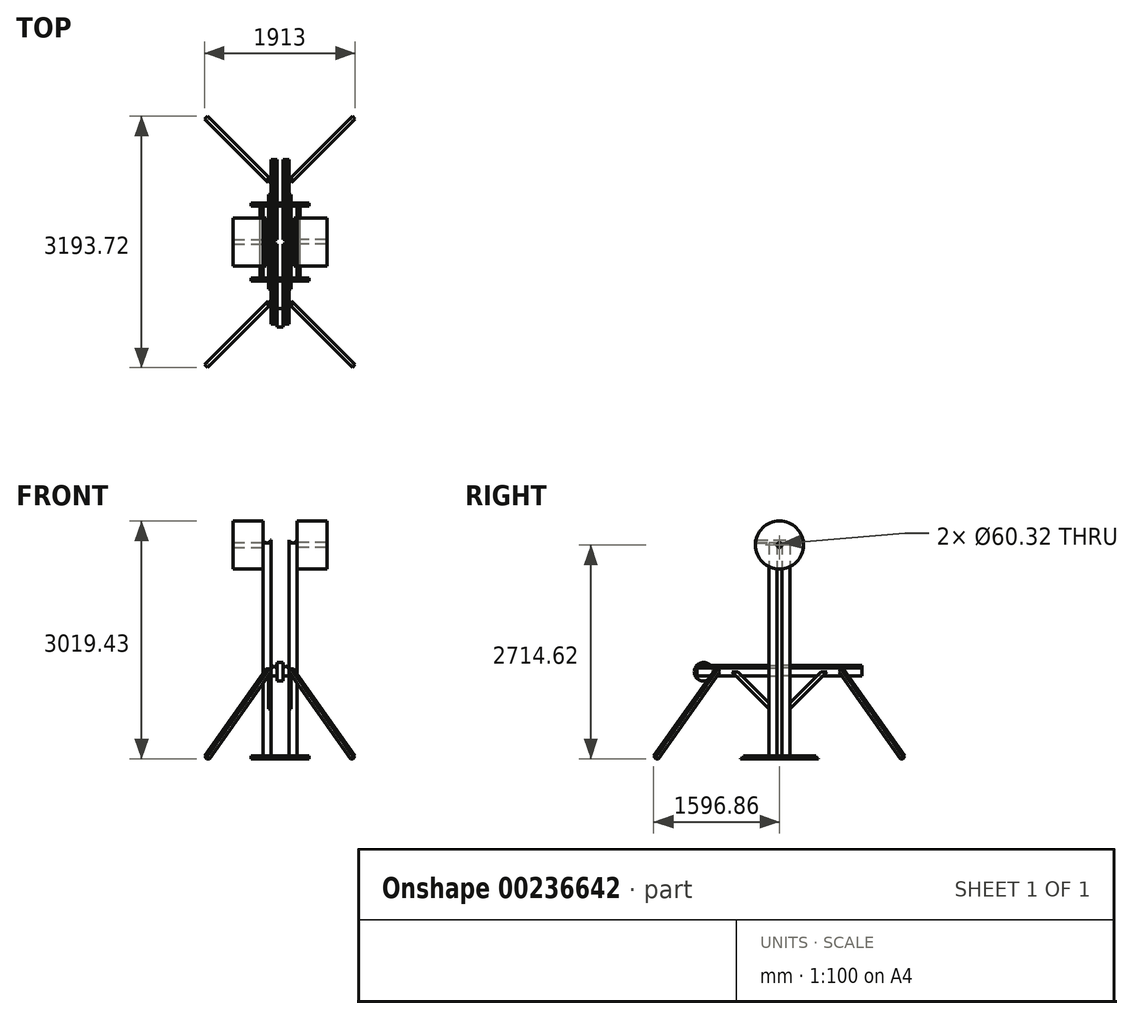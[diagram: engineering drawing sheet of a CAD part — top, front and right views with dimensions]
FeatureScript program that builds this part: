
annotation { "Feature Type Name" : "Feature", "Feature Type Description" : "" }
export const myFeature = defineFeature(function(context is Context, id is Id, definition is map)
    precondition{}
    {
        {
            var Q0;
            Q0=qCreatedBy(makeId("Top.planeOp"),FACE);
            var sketch = newSketch(context, id + "F0", { "sketchPlane" : qUnion([Q0])});
            skLineSegment(sketch, "E0.bottom", {"start": v(114.3, 30.16) * mm, "end": v(215.9, 30.16) * mm});
            skLineSegment(sketch, "E0.top", {"start": v(114.3, 131.76) * mm, "end": v(215.9, 131.76) * mm});
            skLineSegment(sketch, "E0.left", {"start": v(114.3, 30.16) * mm, "end": v(114.3, 131.76) * mm});
            skLineSegment(sketch, "E0.right", {"start": v(215.9, 30.16) * mm, "end": v(215.9, 131.76) * mm});
            skLineSegment(sketch, "E1.MirrorCS", {"start": v(-114.3, 30.16) * mm, "end": v(-215.9, 30.16) * mm});
            skLineSegment(sketch, "E2.MirrorCS", {"start": v(-114.3, 131.76) * mm, "end": v(-215.9, 131.76) * mm});
            skLineSegment(sketch, "E3.MirrorCS", {"start": v(-114.3, 30.16) * mm, "end": v(-114.3, 131.76) * mm});
            skLineSegment(sketch, "E4.MirrorCS", {"start": v(-215.9, 30.16) * mm, "end": v(-215.9, 131.76) * mm});
            skLineSegment(sketch, "E5.MirrorCS", {"start": v(-215.9, -30.16) * mm, "end": v(-215.9, -131.76) * mm});
            skLineSegment(sketch, "E6.MirrorCS", {"start": v(-114.3, -30.16) * mm, "end": v(-114.3, -131.76) * mm});
            skLineSegment(sketch, "E7.MirrorCS", {"start": v(114.3, -30.16) * mm, "end": v(215.9, -30.16) * mm});
            skLineSegment(sketch, "E8.MirrorCS", {"start": v(-114.3, -131.76) * mm, "end": v(-215.9, -131.76) * mm});
            skLineSegment(sketch, "E9.MirrorCS", {"start": v(-114.3, -30.16) * mm, "end": v(-215.9, -30.16) * mm});
            skLineSegment(sketch, "E10.MirrorCS", {"start": v(215.9, -30.16) * mm, "end": v(215.9, -131.76) * mm});
            skLineSegment(sketch, "E11.MirrorCS", {"start": v(114.3, -131.76) * mm, "end": v(215.9, -131.76) * mm});
            skLineSegment(sketch, "E12.MirrorCS", {"start": v(114.3, -30.16) * mm, "end": v(114.3, -131.76) * mm});
            skSolve(sketch);
        }
        {
            var Q0;
            Q0=makeQuery(id+"F0.imprint","IMPRINT",FACE,{"disambiguationData":[TD([[makeQuery(id+"F0.imprint","IMPRINT",EDGE,{"derivedFrom":sQuery(id+"F0.wireOp",EDGE,"E5.MirrorCS")}),1.0]])]});
            var Q1;
            Q1=makeQuery(id+"F0.imprint","IMPRINT",FACE,{"disambiguationData":[TD([[makeQuery(id+"F0.imprint","IMPRINT",EDGE,{"derivedFrom":sQuery(id+"F0.wireOp",EDGE,"E1.MirrorCS")}),-1.0]])]});
            var Q2;
            Q2=makeQuery(id+"F0.imprint","IMPRINT",FACE,{"disambiguationData":[TD([[makeQuery(id+"F0.imprint","IMPRINT",EDGE,{"derivedFrom":sQuery(id+"F0.wireOp",EDGE,"E0.bottom")}),1.0]])]});
            var Q3;
            Q3=makeQuery(id+"F0.imprint","IMPRINT",FACE,{"disambiguationData":[TD([[makeQuery(id+"F0.imprint","IMPRINT",EDGE,{"derivedFrom":sQuery(id+"F0.wireOp",EDGE,"E7.MirrorCS")}),-1.0]])]});
            extrude(context, id + "F1", {"entities" : qUnion([Q0, Q1, Q2, Q3]), "depth" : 2743.2 * mm});
        }
        {
            var Q0;
            Q0=makeQuery(id+"F1.opExtrude","SWEPT_FACE",FACE,{"disambiguationData":[OSD([sQuery(id+"F0.wireOp",EDGE,"E0.bottom")])]});
            var sketch = newSketch(context, id + "F2", { "sketchPlane" : qUnion([Q0])});
            skLineSegment(sketch, "E13.bottom", {"start": v(114.3, 1155.7) * mm, "end": v(38.1, 1155.7) * mm});
            skLineSegment(sketch, "E13.top", {"start": v(114.3, 1054.1) * mm, "end": v(38.1, 1054.1) * mm});
            skLineSegment(sketch, "E13.left", {"start": v(114.3, 1155.7) * mm, "end": v(114.3, 1054.1) * mm});
            skLineSegment(sketch, "E13.right", {"start": v(38.1, 1155.7) * mm, "end": v(38.1, 1054.1) * mm});
            skLineSegment(sketch, "E14", {"start": v(0, 1227.15) * mm, "end": v(0, 1056.68) * mm, "construction": true});
            skLineSegment(sketch, "E15.MirrorCS", {"start": v(-114.3, 1155.7) * mm, "end": v(-38.1, 1155.7) * mm});
            skLineSegment(sketch, "E16.MirrorCS", {"start": v(-114.3, 1054.1) * mm, "end": v(-38.1, 1054.1) * mm});
            skLineSegment(sketch, "E17.MirrorCS", {"start": v(-114.3, 1155.7) * mm, "end": v(-114.3, 1054.1) * mm});
            skLineSegment(sketch, "E18.MirrorCS", {"start": v(-38.1, 1155.7) * mm, "end": v(-38.1, 1054.1) * mm});
            skLineSegment(sketch, "E19", {"start": v(47.72, 1155.7) * mm, "end": v(74.66, 1182.64) * mm});
            skLineSegment(sketch, "E20", {"start": v(74.66, 1182.64) * mm, "end": v(101.6, 1155.7) * mm});
            skLineSegment(sketch, "E21.MirrorCS", {"start": v(-47.72, 1155.7) * mm, "end": v(-74.66, 1182.64) * mm});
            skLineSegment(sketch, "E22.MirrorCS", {"start": v(-74.66, 1182.64) * mm, "end": v(-101.6, 1155.7) * mm});
            skSolve(sketch);
        }
        {
            var Q0;
            Q0=makeQuery(id+"F2.imprint","IMPRINT",FACE,{"disambiguationData":[TD([[makeQuery(id+"F2.imprint","IMPRINT",EDGE,{"derivedFrom":sQuery(id+"F2.wireOp",EDGE,"E15.MirrorCS")}),-1.0]])]});
            var Q1;
            Q1=makeQuery(id+"F2.imprint","IMPRINT",FACE,{"disambiguationData":[TD([[makeQuery(id+"F2.imprint","IMPRINT",EDGE,{"derivedFrom":sQuery(id+"F2.wireOp",EDGE,"E13.bottom")}),1.0]])]});
            var Q2;
            {var subQ0=sQuery(id+"F2.wireOp",EDGE,"E21.MirrorCS");Q2=makeQuery(id+"F2.imprint","IMPRINT",FACE,{"disambiguationData":[TD([[makeQuery(id+"F2.imprint","IMPRINT",EDGE,{"derivedFrom":subQ0}),1.0]])]});}
            var Q3;
            {var subQ0=sQuery(id+"F2.wireOp",EDGE,"E19");Q3=makeQuery(id+"F2.imprint","IMPRINT",FACE,{"disambiguationData":[TD([[makeQuery(id+"F2.imprint","IMPRINT",EDGE,{"derivedFrom":subQ0}),-1.0]])]});}
            extrude(context, id + "F3", {"entities" : qUnion([Q0, Q1, Q2, Q3]), "oppositeDirection" : true, "depth" : 1016 * mm});
        }
        {
            var Q0;
            Q0=makeQuery(id+"F3.opExtrude","SWEPT_BODY",BODY,{"disambiguationData":[OSD([sQuery(id+"F2.wireOp",EDGE,"E13.bottom"),sQuery(id+"F2.wireOp",EDGE,"E13.top"),sQuery(id+"F2.wireOp",EDGE,"E13.left"),sQuery(id+"F2.wireOp",EDGE,"E13.right"),sQuery(id+"F2.wireOp",EDGE,"E19"),sQuery(id+"F2.wireOp",EDGE,"E20")])]});
            var Q1;
            Q1=makeQuery(id+"F3.opExtrude","SWEPT_BODY",BODY,{"disambiguationData":[OSD([sQuery(id+"F2.wireOp",EDGE,"E15.MirrorCS"),sQuery(id+"F2.wireOp",EDGE,"E16.MirrorCS"),sQuery(id+"F2.wireOp",EDGE,"E17.MirrorCS"),sQuery(id+"F2.wireOp",EDGE,"E18.MirrorCS"),sQuery(id+"F2.wireOp",EDGE,"E21.MirrorCS"),sQuery(id+"F2.wireOp",EDGE,"E22.MirrorCS")])]});
            var Q2;
            Q2=qCreatedBy(makeId("Front.planeOp"),FACE);
            mirror(context, id + "F4", {"entities" : qUnion([Q0, Q1]), "mirrorPlane" : qUnion([Q2])});
        }
        {
            var Q0;
            Q0=makeQuery(id+"F4.opPattern","COPY",FACE,{"derivedFrom":makeQuery(id+"F3.opExtrude","SWEPT_FACE",FACE,{"disambiguationData":[OSD([sQuery(id+"F2.wireOp",EDGE,"E18.MirrorCS")])]}),"instanceName":"1"});
            var sketch = newSketch(context, id + "F5", { "sketchPlane" : qUnion([Q0])});
            skCircle(sketch, "E23", {"center": v(-965.2, 1104.9) * mm, "radius": 117.48 * mm});
            skSolve(sketch);
        }
        {
            var Q0;
            {var subQ1=sQuery(id+"F2.wireOp",EDGE,"E18.MirrorCS");var subQ6=makeQuery(id+"F4.opPattern","COPY",EDGE,{"derivedFrom":makeQuery(id+"F3.opExtrude","CAP_EDGE",EDGE,{"disambiguationData":[OSD([subQ1])],"isStart":false}),"instanceName":"1"});Q0=makeQuery(id+"F5.imprint","IMPRINT",FACE,{"disambiguationData":[TD([[makeQuery(id+"F5.imprint","IMPRINT",EDGE,{"derivedFrom":subQ6}),-1.0]])]});}
            var Q1;
            {var subQ1=sQuery(id+"F2.wireOp",EDGE,"E18.MirrorCS");var subQ6=makeQuery(id+"F4.opPattern","COPY",EDGE,{"derivedFrom":makeQuery(id+"F3.opExtrude","CAP_EDGE",EDGE,{"disambiguationData":[OSD([subQ1])],"isStart":false}),"instanceName":"1"});Q1=makeQuery(id+"F5.imprint","IMPRINT",FACE,{"disambiguationData":[TD([[makeQuery(id+"F5.imprint","IMPRINT",EDGE,{"derivedFrom":subQ6}),1.0]])]});}
            extrude(context, id + "F6", {"entities" : qUnion([Q0, Q1]), "depth" : 76.2 * mm});
        }
        {
            var Q0;
            Q0=makeQuery(id+"F4.opPattern","COPY",FACE,{"derivedFrom":makeQuery(id+"F3.opExtrude","SWEPT_FACE",FACE,{"disambiguationData":[OSD([sQuery(id+"F2.wireOp",EDGE,"E13.left")])]}),"instanceName":"1"});
            var sketch = newSketch(context, id + "F7", { "sketchPlane" : qUnion([Q0])});
            skLineSegment(sketch, "E24.0", {"start": v(-131.76, 2743.2) * mm, "end": v(-131.76, 0) * mm, "construction": true});
            skLineSegment(sketch, "E25", {"start": v(-564.5, 1104.9) * mm, "end": v(-486.45, 1104.9) * mm, "construction": true});
            skLineSegment(sketch, "E26", {"start": v(-564.5, 1104.9) * mm, "end": v(-564.5, 1155.7) * mm, "construction": true});
            skLineSegment(sketch, "E27", {"start": v(-564.5, 1104.9) * mm, "end": v(-564.5, 1054.1) * mm, "construction": true});
            skLineSegment(sketch, "E28", {"start": v(-131.76, 635) * mm, "end": v(-601.66, 1104.9) * mm});
            skLineSegment(sketch, "E29", {"start": v(-601.66, 1104.9) * mm, "end": v(-525.47, 1104.9) * mm});
            skLineSegment(sketch, "E30", {"start": v(-525.47, 1104.9) * mm, "end": v(-131.76, 711.19) * mm});
            skLineSegment(sketch, "E31", {"start": v(-131.76, 711.19) * mm, "end": v(-131.76, 635) * mm});
            skSolve(sketch);
        }
        {
            var Q0;
            {var subQ0=sQuery(id+"F7.wireOp",EDGE,"E31");Q0=makeQuery(id+"F7.imprint","IMPRINT",FACE,{"disambiguationData":[TD([[makeQuery(id+"F7.imprint","IMPRINT",EDGE,{"derivedFrom":subQ0}),-1.0]])]});}
            var Q1;
            {var subQ0=sQuery(id+"F7.wireOp",EDGE,"E29");Q1=makeQuery(id+"F7.imprint","IMPRINT",FACE,{"disambiguationData":[TD([[makeQuery(id+"F7.imprint","IMPRINT",EDGE,{"derivedFrom":subQ0}),-1.0]])]});}
            extrude(context, id + "F8", {"entities" : qUnion([Q0, Q1]), "depth" : 26.92 * mm});
        }
        {
            var Q0;
            Q0=makeQuery(id+"FNKVfird8vsgjME_14.opPattern","COPY",BODY,{"derivedFrom":makeQuery(id+"F8.opExtrude","SWEPT_BODY",BODY,{"disambiguationData":[OSD([sQuery(id+"F7.wireOp",EDGE,"E28"),sQuery(id+"F7.wireOp",EDGE,"E29"),sQuery(id+"F7.wireOp",EDGE,"E30"),sQuery(id+"F7.wireOp",EDGE,"E31")])]}),"instanceName":"1"});
            var Q1;
            Q1=makeQuery(id+"F8.opExtrude","SWEPT_BODY",BODY,{"disambiguationData":[OSD([sQuery(id+"F7.wireOp",EDGE,"E28"),sQuery(id+"F7.wireOp",EDGE,"E29"),sQuery(id+"F7.wireOp",EDGE,"E30"),sQuery(id+"F7.wireOp",EDGE,"E31")])]});
            var Q2;
            Q2=qCreatedBy(makeId("Front.planeOp"),FACE);
            mirror(context, id + "F9", {"entities" : qUnion([Q0, Q1]), "mirrorPlane" : qUnion([Q2])});
        }
        {
            var Q0;
            Q0=makeQuery(id+"F8.opExtrude","SWEPT_BODY",BODY,{"disambiguationData":[OSD([sQuery(id+"F7.wireOp",EDGE,"E28"),sQuery(id+"F7.wireOp",EDGE,"E29"),sQuery(id+"F7.wireOp",EDGE,"E30"),sQuery(id+"F7.wireOp",EDGE,"E31")])]});
            var Q1;
            Q1=makeQuery(id+"FNKVfird8vsgjME_14.opPattern","COPY",BODY,{"derivedFrom":makeQuery(id+"F8.opExtrude","SWEPT_BODY",BODY,{"disambiguationData":[OSD([sQuery(id+"F7.wireOp",EDGE,"E28"),sQuery(id+"F7.wireOp",EDGE,"E29"),sQuery(id+"F7.wireOp",EDGE,"E30"),sQuery(id+"F7.wireOp",EDGE,"E31")])]}),"instanceName":"1"});
            var Q2;
            Q2=makeQuery(id+"F9.opPattern","COPY",BODY,{"derivedFrom":makeQuery(id+"FNKVfird8vsgjME_14.opPattern","COPY",BODY,{"derivedFrom":makeQuery(id+"F8.opExtrude","SWEPT_BODY",BODY,{"disambiguationData":[OSD([sQuery(id+"F7.wireOp",EDGE,"E28"),sQuery(id+"F7.wireOp",EDGE,"E29"),sQuery(id+"F7.wireOp",EDGE,"E30"),sQuery(id+"F7.wireOp",EDGE,"E31")])]}),"instanceName":"1"}),"instanceName":"1"});
            var Q3;
            Q3=makeQuery(id+"F9.opPattern","COPY",BODY,{"derivedFrom":makeQuery(id+"F8.opExtrude","SWEPT_BODY",BODY,{"disambiguationData":[OSD([sQuery(id+"F7.wireOp",EDGE,"E28"),sQuery(id+"F7.wireOp",EDGE,"E29"),sQuery(id+"F7.wireOp",EDGE,"E30"),sQuery(id+"F7.wireOp",EDGE,"E31")])]}),"instanceName":"1"});
            var Q4;
            Q4=qCreatedBy(makeId("Right.planeOp"),FACE);
            mirror(context, id + "F10", {"entities" : qUnion([Q0, Q1, Q2, Q3]), "mirrorPlane" : qUnion([Q4])});
        }
        {
            var Q0;
            Q0=qCreatedBy(makeId("Front.planeOp"),FACE);
            var sketch = newSketch(context, id + "F11", { "sketchPlane" : qUnion([Q0])});
            skLineSegment(sketch, "E32.0", {"start": v(114.3, 2743.2) * mm, "end": v(114.3, 0) * mm, "construction": true});
            skLineSegment(sketch, "E32.1", {"start": v(-114.3, 2743.2) * mm, "end": v(-114.3, 0) * mm, "construction": true});
            skLineSegment(sketch, "E32.2", {"start": v(-215.9, 2743.2) * mm, "end": v(-215.9, 0) * mm, "construction": true});
            skLineSegment(sketch, "E32.3", {"start": v(215.9, 2743.2) * mm, "end": v(215.9, 0) * mm, "construction": true});
            skLineSegment(sketch, "E33", {"start": v(-114.3, 0) * mm, "end": v(-114.3, 38.1) * mm});
            skLineSegment(sketch, "E34", {"start": v(-114.3, 38.1) * mm, "end": v(-111.12, 38.1) * mm});
            skLineSegment(sketch, "E35", {"start": v(-111.12, 38.1) * mm, "end": v(-111.12, 3.18) * mm});
            skLineSegment(sketch, "E36", {"start": v(-111.12, 3.18) * mm, "end": v(-76.2, 3.18) * mm});
            skLineSegment(sketch, "E37", {"start": v(-76.2, 3.18) * mm, "end": v(-76.2, 0) * mm});
            skLineSegment(sketch, "E38", {"start": v(-76.2, 0) * mm, "end": v(-114.3, 0) * mm});
            skLineSegment(sketch, "E39", {"start": v(-215.9, 0) * mm, "end": v(-215.9, 38.1) * mm});
            skLineSegment(sketch, "E40", {"start": v(-215.9, 38.1) * mm, "end": v(-219.07, 38.1) * mm});
            skLineSegment(sketch, "E41", {"start": v(-219.07, 38.1) * mm, "end": v(-219.07, 3.17) * mm});
            skLineSegment(sketch, "E42", {"start": v(-219.07, 3.17) * mm, "end": v(-254, 3.17) * mm});
            skLineSegment(sketch, "E43", {"start": v(-254, 3.17) * mm, "end": v(-254, 0) * mm});
            skLineSegment(sketch, "E44", {"start": v(-254, 0) * mm, "end": v(-215.9, 0) * mm});
            skLineSegment(sketch, "E45.MirrorCS", {"start": v(114.3, 0) * mm, "end": v(114.3, 38.1) * mm});
            skLineSegment(sketch, "E46.MirrorCS", {"start": v(111.12, 38.1) * mm, "end": v(111.12, 3.18) * mm});
            skLineSegment(sketch, "E47.MirrorCS", {"start": v(76.2, 0) * mm, "end": v(114.3, 0) * mm});
            skLineSegment(sketch, "E48.MirrorCS", {"start": v(111.12, 3.18) * mm, "end": v(76.2, 3.18) * mm});
            skLineSegment(sketch, "E49.MirrorCS", {"start": v(76.2, 3.18) * mm, "end": v(76.2, 0) * mm});
            skLineSegment(sketch, "E50.MirrorCS", {"start": v(114.3, 38.1) * mm, "end": v(111.12, 38.1) * mm});
            skLineSegment(sketch, "E51.MirrorCS", {"start": v(254, 3.17) * mm, "end": v(254, 0) * mm});
            skLineSegment(sketch, "E52.MirrorCS", {"start": v(215.9, 38.1) * mm, "end": v(219.07, 38.1) * mm});
            skLineSegment(sketch, "E53.MirrorCS", {"start": v(215.9, 0) * mm, "end": v(215.9, 38.1) * mm});
            skLineSegment(sketch, "E54.MirrorCS", {"start": v(219.07, 3.17) * mm, "end": v(254, 3.17) * mm});
            skLineSegment(sketch, "E55.MirrorCS", {"start": v(254, 0) * mm, "end": v(215.9, 0) * mm});
            skLineSegment(sketch, "E56.MirrorCS", {"start": v(219.07, 38.1) * mm, "end": v(219.07, 3.17) * mm});
            skSolve(sketch);
        }
        {
            var Q0;
            Q0=makeQuery(id+"F11.imprint","IMPRINT",FACE,{"disambiguationData":[TD([[makeQuery(id+"F11.imprint","IMPRINT",EDGE,{"derivedFrom":sQuery(id+"F11.wireOp",EDGE,"E39")}),1.0]])]});
            var Q1;
            Q1=makeQuery(id+"F11.imprint","IMPRINT",FACE,{"disambiguationData":[TD([[makeQuery(id+"F11.imprint","IMPRINT",EDGE,{"derivedFrom":sQuery(id+"F11.wireOp",EDGE,"E33")}),-1.0]])]});
            var Q2;
            Q2=makeQuery(id+"F11.imprint","IMPRINT",FACE,{"disambiguationData":[TD([[makeQuery(id+"F11.imprint","IMPRINT",EDGE,{"derivedFrom":sQuery(id+"F11.wireOp",EDGE,"E49.MirrorCS")}),1.0]])]});
            var Q3;
            Q3=makeQuery(id+"F11.imprint","IMPRINT",FACE,{"disambiguationData":[TD([[makeQuery(id+"F11.imprint","IMPRINT",EDGE,{"derivedFrom":sQuery(id+"F11.wireOp",EDGE,"E51.MirrorCS")}),-1.0]])]});
            extrude(context, id + "F12", {"entities" : qUnion([Q0, Q1, Q2, Q3]), "depth" : 914.4 * mm, "symmetric" : true});
        }
        {
            var Q0;
            Q0=qCreatedBy(makeId("Right.planeOp"),FACE);
            var sketch = newSketch(context, id + "F13", { "sketchPlane" : qUnion([Q0])});
            skLineSegment(sketch, "E57.0", {"start": v(-457.2, 0) * mm, "end": v(-457.2, 38.1) * mm});
            skLineSegment(sketch, "E58", {"start": v(-457.2, 38.1) * mm, "end": v(-460.38, 38.1) * mm});
            skLineSegment(sketch, "E59", {"start": v(-460.38, 38.1) * mm, "end": v(-460.38, 3.18) * mm});
            skLineSegment(sketch, "E60", {"start": v(-460.38, 3.18) * mm, "end": v(-495.3, 3.17) * mm});
            skLineSegment(sketch, "E61", {"start": v(-495.3, 3.17) * mm, "end": v(-495.3, 0) * mm});
            skLineSegment(sketch, "E62", {"start": v(-495.3, 0) * mm, "end": v(-457.2, 0) * mm});
            skLineSegment(sketch, "E63.MirrorCS", {"start": v(495.3, 3.17) * mm, "end": v(495.3, 0) * mm});
            skLineSegment(sketch, "E64.MirrorCS", {"start": v(457.2, 38.1) * mm, "end": v(460.38, 38.1) * mm});
            skLineSegment(sketch, "E65.MirrorCS", {"start": v(460.38, 3.18) * mm, "end": v(495.3, 3.17) * mm});
            skLineSegment(sketch, "E66.MirrorCS", {"start": v(460.38, 38.1) * mm, "end": v(460.38, 3.18) * mm});
            skLineSegment(sketch, "E67.MirrorCS", {"start": v(457.2, 0) * mm, "end": v(457.2, 38.1) * mm});
            skLineSegment(sketch, "E68.MirrorCS", {"start": v(495.3, 0) * mm, "end": v(457.2, 0) * mm});
            skSolve(sketch);
        }
        {
            var Q0;
            Q0=makeQuery(id+"F13.imprint","IMPRINT",FACE,{"disambiguationData":[TD([[makeQuery(id+"F13.imprint","IMPRINT",EDGE,{"derivedFrom":sQuery(id+"F13.wireOp",EDGE,"E57.0")}),1.0]])]});
            var Q1;
            Q1=makeQuery(id+"F13.imprint","IMPRINT",FACE,{"disambiguationData":[TD([[makeQuery(id+"F13.imprint","IMPRINT",EDGE,{"derivedFrom":sQuery(id+"F13.wireOp",EDGE,"E63.MirrorCS")}),-1.0]])]});
            extrude(context, id + "F14", {"entities" : qUnion([Q0, Q1]), "depth" : 736.6 * mm, "symmetric" : true});
        }
        {
            var Q0;
            Q0=makeQuery(id+"F1.opExtrude","SWEPT_FACE",FACE,{"disambiguationData":[OSD([sQuery(id+"F0.wireOp",EDGE,"E0.right")])]});
            var sketch = newSketch(context, id + "F15", { "sketchPlane" : qUnion([Q0])});
            skCircle(sketch, "E69", {"center": v(0, 2714.63) * mm, "radius": 30.16 * mm});
            skCircle(sketch, "E70", {"center": v(0, 2714.63) * mm, "radius": 304.8 * mm});
            skSolve(sketch);
        }
        {
            var Q0;
            Q0=qCreatedBy(makeId("Front.planeOp"),FACE);
            var sketch = newSketch(context, id + "F16", { "sketchPlane" : qUnion([Q0])});
            skLineSegment(sketch, "E71.0", {"start": v(-114.3, 2743.2) * mm, "end": v(-215.9, 2743.2) * mm, "construction": true});
            skLineSegment(sketch, "E72.0", {"start": v(114.3, 2743.2) * mm, "end": v(215.9, 2743.2) * mm, "construction": true});
            skLineSegment(sketch, "E73", {"start": v(-215.9, 2743.2) * mm, "end": v(-215.9, 2781.3) * mm});
            skLineSegment(sketch, "E74", {"start": v(-215.9, 2781.3) * mm, "end": v(-212.72, 2781.3) * mm});
            skLineSegment(sketch, "E75", {"start": v(-212.72, 2781.3) * mm, "end": v(-212.72, 2746.38) * mm});
            skLineSegment(sketch, "E76", {"start": v(-212.72, 2746.38) * mm, "end": v(-177.8, 2746.38) * mm});
            skLineSegment(sketch, "E77", {"start": v(-177.8, 2746.38) * mm, "end": v(-177.8, 2743.2) * mm});
            skLineSegment(sketch, "E78", {"start": v(-177.8, 2743.2) * mm, "end": v(-215.9, 2743.2) * mm});
            skLineSegment(sketch, "E79", {"start": v(-114.3, 2743.2) * mm, "end": v(-152.4, 2743.2) * mm});
            skLineSegment(sketch, "E80", {"start": v(-152.4, 2743.2) * mm, "end": v(-152.4, 2746.38) * mm});
            skLineSegment(sketch, "E81", {"start": v(-152.4, 2746.38) * mm, "end": v(-117.47, 2746.38) * mm});
            skLineSegment(sketch, "E82", {"start": v(-117.47, 2746.38) * mm, "end": v(-117.47, 2781.3) * mm});
            skLineSegment(sketch, "E83", {"start": v(-117.47, 2781.3) * mm, "end": v(-114.3, 2781.3) * mm});
            skLineSegment(sketch, "E84", {"start": v(-114.3, 2781.3) * mm, "end": v(-114.3, 2743.2) * mm});
            skLineSegment(sketch, "E85.MirrorCS", {"start": v(152.4, 2743.2) * mm, "end": v(152.4, 2746.38) * mm});
            skLineSegment(sketch, "E86.MirrorCS", {"start": v(117.47, 2781.3) * mm, "end": v(114.3, 2781.3) * mm});
            skLineSegment(sketch, "E87.MirrorCS", {"start": v(177.8, 2746.38) * mm, "end": v(177.8, 2743.2) * mm});
            skLineSegment(sketch, "E88.MirrorCS", {"start": v(114.3, 2781.3) * mm, "end": v(114.3, 2743.2) * mm});
            skLineSegment(sketch, "E89.MirrorCS", {"start": v(117.47, 2746.38) * mm, "end": v(117.47, 2781.3) * mm});
            skLineSegment(sketch, "E90.MirrorCS", {"start": v(152.4, 2746.38) * mm, "end": v(117.47, 2746.38) * mm});
            skLineSegment(sketch, "E91.MirrorCS", {"start": v(114.3, 2743.2) * mm, "end": v(152.4, 2743.2) * mm});
            skLineSegment(sketch, "E92.MirrorCS", {"start": v(215.9, 2781.3) * mm, "end": v(212.72, 2781.3) * mm});
            skLineSegment(sketch, "E93.MirrorCS", {"start": v(215.9, 2743.2) * mm, "end": v(215.9, 2781.3) * mm});
            skLineSegment(sketch, "E94.MirrorCS", {"start": v(212.72, 2781.3) * mm, "end": v(212.72, 2746.38) * mm});
            skLineSegment(sketch, "E95.MirrorCS", {"start": v(212.72, 2746.38) * mm, "end": v(177.8, 2746.38) * mm});
            skLineSegment(sketch, "E96.MirrorCS", {"start": v(177.8, 2743.2) * mm, "end": v(215.9, 2743.2) * mm});
            skSolve(sketch);
        }
        {
            var Q0;
            Q0=makeQuery(id+"F16.imprint","IMPRINT",FACE,{"disambiguationData":[TD([[makeQuery(id+"F16.imprint","IMPRINT",EDGE,{"derivedFrom":sQuery(id+"F16.wireOp",EDGE,"E85.MirrorCS")}),1.0]])]});
            var Q1;
            Q1=makeQuery(id+"F16.imprint","IMPRINT",FACE,{"disambiguationData":[TD([[makeQuery(id+"F16.imprint","IMPRINT",EDGE,{"derivedFrom":sQuery(id+"F16.wireOp",EDGE,"E92.MirrorCS")}),1.0]])]});
            var Q2;
            Q2=makeQuery(id+"F16.imprint","IMPRINT",FACE,{"disambiguationData":[TD([[makeQuery(id+"F16.imprint","IMPRINT",EDGE,{"derivedFrom":sQuery(id+"F16.wireOp",EDGE,"E73")}),-1.0]])]});
            var Q3;
            Q3=makeQuery(id+"F16.imprint","IMPRINT",FACE,{"disambiguationData":[TD([[makeQuery(id+"F16.imprint","IMPRINT",EDGE,{"derivedFrom":sQuery(id+"F16.wireOp",EDGE,"E79")}),-1.0]])]});
            extrude(context, id + "F17", {"entities" : qUnion([Q0, Q1, Q2, Q3]), "depth" : 609.6 * mm, "symmetric" : true});
        }
        {
            var Q0;
            {var subQ0=sQuery(id+"F0.wireOp",EDGE,"E0.right");var subQ5=makeQuery(id+"F1.opExtrude","CAP_EDGE",EDGE,{"disambiguationData":[OSD([subQ0])],"isStart":false});Q0=makeQuery(id+"F15.imprint","IMPRINT",FACE,{"disambiguationData":[TD([[makeQuery(id+"F15.imprint","IMPRINT",EDGE,{"derivedFrom":subQ5}),-1.0]])]});}
            var Q1;
            {var subQ0=sQuery(id+"F0.wireOp",EDGE,"E0.right");var subQ5=makeQuery(id+"F1.opExtrude","CAP_EDGE",EDGE,{"disambiguationData":[OSD([subQ0])],"isStart":false});Q1=makeQuery(id+"F15.imprint","IMPRINT",FACE,{"disambiguationData":[TD([[makeQuery(id+"F15.imprint","IMPRINT",EDGE,{"derivedFrom":subQ5}),1.0]])]});}
            extrude(context, id + "F18", {"entities" : qUnion([Q0, Q1]), "depth" : 381 * mm});
        }
        {
            var Q0;
            Q0=makeQuery(id+"F18.opExtrude","SWEPT_BODY",BODY,{"disambiguationData":[OSD([sQuery(id+"F15.wireOp",EDGE,"E70")])]});
            var Q1;
            Q1=qCreatedBy(makeId("Right.planeOp"),FACE);
            mirror(context, id + "F19", {"entities" : qUnion([Q0]), "mirrorPlane" : qUnion([Q1])});
        }
        {
            var Q0;
            Q0=makeQuery(id+"F12.opExtrude","CAP_EDGE",EDGE,{"disambiguationData":[OSD([sQuery(id+"F11.wireOp",EDGE,"E56.MirrorCS")])],"isStart":false});
            cPlane(context, id + "F20", {"entities" : qUnion([Q0]), "cplaneType" : CPlaneType.LINE_ANGLE, "offset" : 25.4 * mm, "angle" : 45 * degree, "width" : 152.4 * mm, "height" : 152.4 * mm});
        }
        {
            var Q0;
            Q0=qCreatedBy(id+"F20.planeOp",FACE);
            var sketch = newSketch(context, id + "F21", { "sketchPlane" : qUnion([Q0])});
            skLineSegment(sketch, "E97.0", {"start": v(820.57, 1054.1) * mm, "end": v(102.15, 1054.1) * mm, "construction": true});
            skLineSegment(sketch, "E98.0", {"start": v(502.9, 0) * mm, "end": v(-143.68, 0) * mm, "construction": true});
            skLineSegment(sketch, "E99", {"start": v(502.9, 0) * mm, "end": v(2416.7, 0) * mm, "construction": true});
            skLineSegment(sketch, "E100", {"start": v(639.28, 1104.9) * mm, "end": v(1744.18, 0) * mm});
            skLineSegment(sketch, "E101", {"start": v(639.28, 1104.9) * mm, "end": v(675.2, 1140.82) * mm});
            skLineSegment(sketch, "E102", {"start": v(675.2, 1140.82) * mm, "end": v(1780.1, 35.92) * mm});
            skLineSegment(sketch, "E103", {"start": v(1744.18, 0) * mm, "end": v(1780.1, 35.92) * mm});
            skSolve(sketch);
        }
        {
            var Q0;
            Q0=makeQuery(id+"F21.imprint","IMPRINT",FACE,{"disambiguationData":[TD([[makeQuery(id+"F21.imprint","IMPRINT",EDGE,{"derivedFrom":sQuery(id+"F21.wireOp",EDGE,"E100")}),1.0]])]});
            extrude(context, id + "F22", {"entities" : qUnion([Q0]), "depth" : 50.8 * mm});
        }
        {
            var Q0;
            Q0=makeQuery(id+"F22.opExtrude","SWEPT_BODY",BODY,{"disambiguationData":[OSD([sQuery(id+"F21.wireOp",EDGE,"E100"),sQuery(id+"F21.wireOp",EDGE,"E101"),sQuery(id+"F21.wireOp",EDGE,"E102"),sQuery(id+"F21.wireOp",EDGE,"E103")])]});
            var Q1;
            Q1=qCreatedBy(makeId("Right.planeOp"),FACE);
            mirror(context, id + "F23", {"entities" : qUnion([Q0]), "mirrorPlane" : qUnion([Q1])});
        }
        {
            var Q0;
            Q0=makeQuery(id+"F22.opExtrude","SWEPT_BODY",BODY,{"disambiguationData":[OSD([sQuery(id+"F21.wireOp",EDGE,"E100"),sQuery(id+"F21.wireOp",EDGE,"E101"),sQuery(id+"F21.wireOp",EDGE,"E102"),sQuery(id+"F21.wireOp",EDGE,"E103")])]});
            var Q1;
            Q1=makeQuery(id+"F23.opPattern","COPY",BODY,{"derivedFrom":makeQuery(id+"F22.opExtrude","SWEPT_BODY",BODY,{"disambiguationData":[OSD([sQuery(id+"F21.wireOp",EDGE,"E100"),sQuery(id+"F21.wireOp",EDGE,"E101"),sQuery(id+"F21.wireOp",EDGE,"E102"),sQuery(id+"F21.wireOp",EDGE,"E103")])]}),"instanceName":"1"});
            var Q2;
            Q2=qCreatedBy(makeId("Front.planeOp"),FACE);
            mirror(context, id + "F24", {"entities" : qUnion([Q0, Q1]), "mirrorPlane" : qUnion([Q2])});
        }
    });
